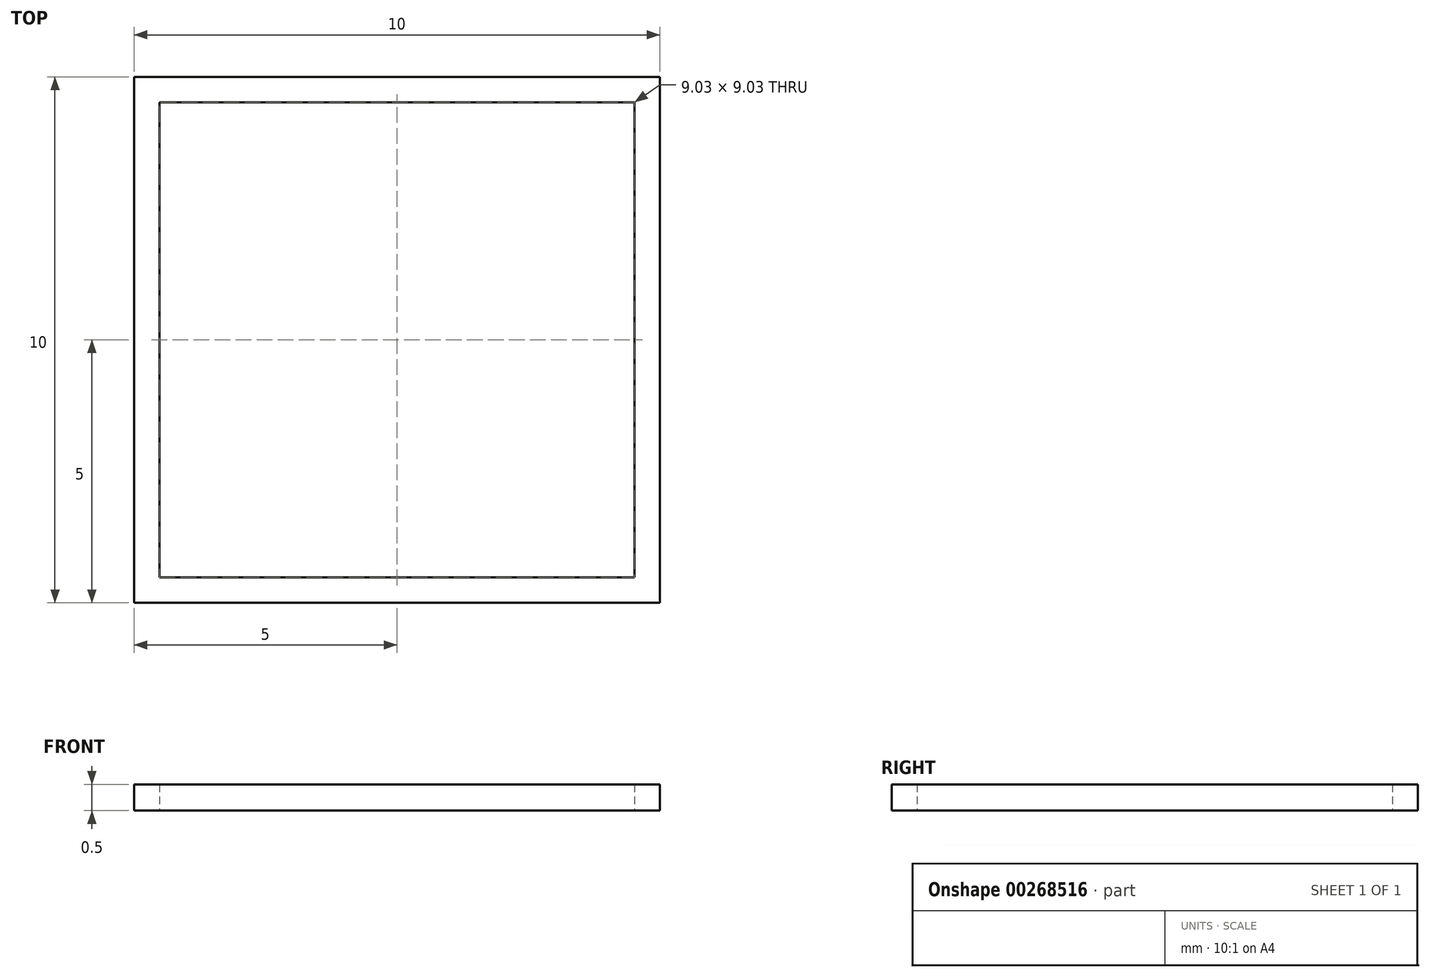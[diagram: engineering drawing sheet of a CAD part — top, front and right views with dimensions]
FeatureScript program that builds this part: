
annotation { "Feature Type Name" : "Feature", "Feature Type Description" : "" }
export const myFeature = defineFeature(function(context is Context, id is Id, definition is map)
    precondition{}
    {
        {
            var Q0;
            Q0=qCreatedBy(makeId("Top.planeOp"),FACE);
            var sketch = newSketch(context, id + "F0", { "sketchPlane" : qUnion([Q0])});
            skLineSegment(sketch, "E0.bottom", {"start": v(0, 0) * mm, "end": v(10, 0) * mm});
            skLineSegment(sketch, "E0.top", {"start": v(0, 10) * mm, "end": v(10, 10) * mm});
            skLineSegment(sketch, "E0.left", {"start": v(0, 0) * mm, "end": v(0, 10) * mm});
            skLineSegment(sketch, "E0.right", {"start": v(10, 0) * mm, "end": v(10, 10) * mm});
            skLineSegment(sketch, "E1.0", {"start": v(0.48, 0.48) * mm, "end": v(0.48, 9.52) * mm});
            skLineSegment(sketch, "E1.1", {"start": v(0.48, 0.48) * mm, "end": v(9.52, 0.48) * mm});
            skLineSegment(sketch, "E1.2", {"start": v(9.52, 0.48) * mm, "end": v(9.52, 9.52) * mm});
            skLineSegment(sketch, "E1.3", {"start": v(0.48, 9.52) * mm, "end": v(9.52, 9.52) * mm});
            skSolve(sketch);
        }
        {
            var Q0;
            Q0=makeQuery(id+"F0.imprint","IMPRINT",FACE,{"disambiguationData":[TD([[makeQuery(id+"F0.imprint","IMPRINT",EDGE,{"derivedFrom":sQuery(id+"F0.wireOp",EDGE,"E0.bottom")}),1.0]])]});
            extrude(context, id + "F1", {"entities" : qUnion([Q0]), "depth" : 0.5 * mm});
        }
    });
